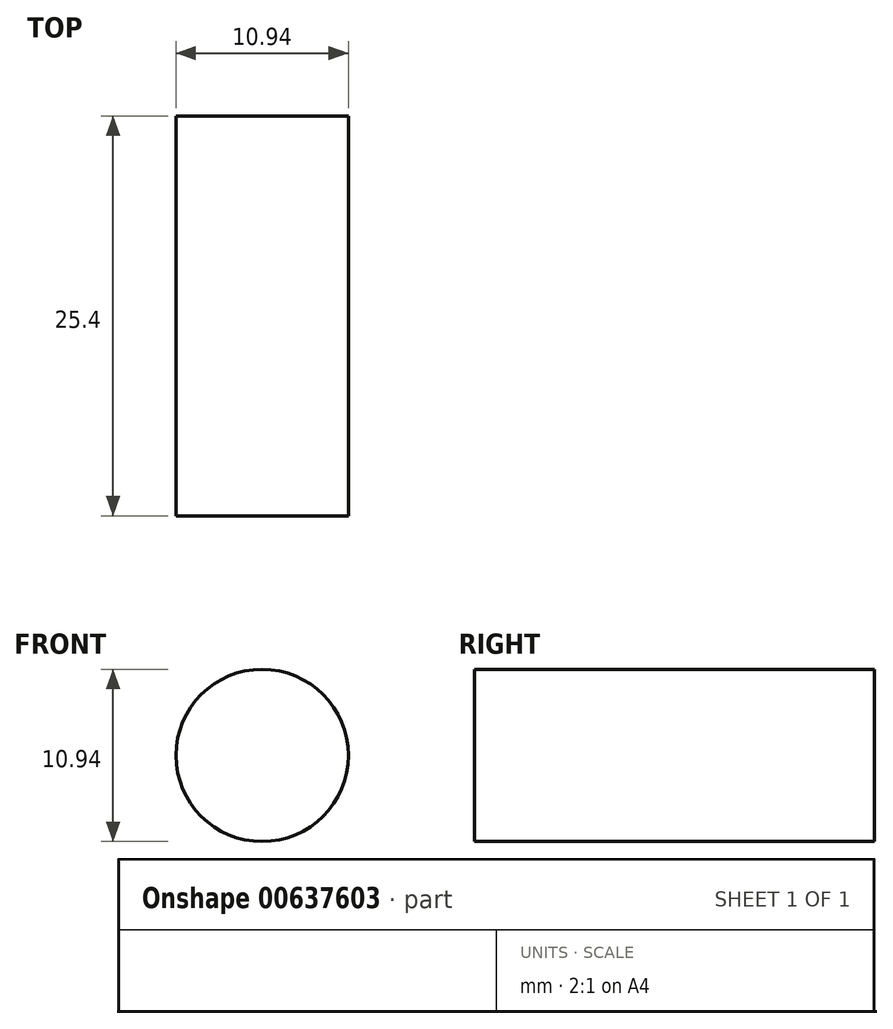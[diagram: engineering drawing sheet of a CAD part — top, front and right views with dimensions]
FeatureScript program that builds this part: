
annotation { "Feature Type Name" : "Feature", "Feature Type Description" : "" }
export const myFeature = defineFeature(function(context is Context, id is Id, definition is map)
    precondition{}
    {
        {
            var Q0;
            Q0=qCreatedBy(makeId("Front.planeOp"),FACE);
            var sketch = newSketch(context, id + "F0", { "sketchPlane" : qUnion([Q0])});
            skCircle(sketch, "E0", {"center": v(0, 0) * mm, "radius": 5.47 * mm});
            skSolve(sketch);
        }
        {
            var Q0;
            Q0 = qSketchRegion(id + "F0", true);
            extrude(context, id + "F1", {"entities" : qUnion([Q0]), "depth" : 25.4 * mm, "offsetDistance" : 25.4 * mm});
        }
    });
